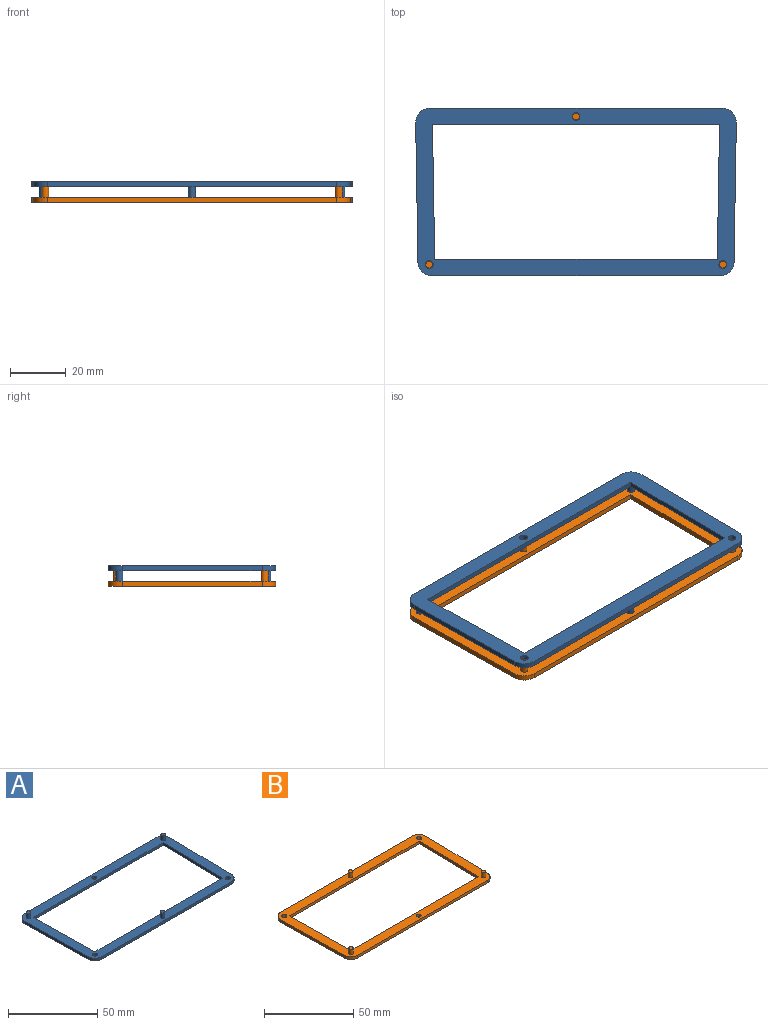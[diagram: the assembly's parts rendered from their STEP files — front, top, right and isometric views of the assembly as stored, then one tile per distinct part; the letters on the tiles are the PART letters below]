
ASSEMBLY  parts=2 mates=1
PART A: 23 faces, bbox 114.8x60x5.4 mm
  f0: plane 104.83x1.8mm, normal (0,1,0), area 188.7mm2, adj f8,f9,f21,f22
  f1: plane 50x1.8mm, normal (-1,-0.02,0), area 90mm2, adj f8,f9,f19,f22
  f2: plane 103.17x1.8mm, normal (0,-1,0), area 185.7mm2, adj f8,f9,f19,f20
  f3: plane 48x1.8mm, normal (1,0.02,0), area 86.4mm2, adj f4,f6,f8,f9
  f4: plane 102.8x1.8mm, normal (0,-1,0), area 185mm2, adj f3,f5,f8,f9
  f5: plane 48x1.8mm, normal (-1,0.02,0), area 86.4mm2, adj f4,f6,f8,f9
  f6: plane 101.2x1.8mm, normal (0,1,0), area 182.2mm2, adj f3,f5,f8,f9
  f7: plane 50x1.8mm, normal (1,-0.02,0), area 90mm2, adj f8,f9,f20,f21
  f8: plane 114.83x60mm, normal (0,0,1), area 1889.4mm2, adj f0,f1,f2,f3,f4,f5,f6,f7
  f9: plane 114.83x60mm, normal (0,0,-1), area 1904.1mm2, adj f0,f1,f2,f3,f4,f5,f6,f7
  f10: cylinder r=1.25mm len=3.6mm, axis (0,0,-1), area 28.3mm2, adj f8,f11
  f11: plane 2.5x2.5mm, normal (0,0,1), area 4.9mm2, adj f10
  f12: cylinder r=1.25mm len=3.6mm, axis (0,0,-1), area 28.3mm2, adj f8,f13
  f13: plane 2.5x2.5mm, normal (0,0,1), area 4.9mm2, adj f12
  f14: cylinder r=1.25mm len=3.6mm, axis (0,0,-1), area 28.3mm2, adj f8,f15
  f15: plane 2.5x2.5mm, normal (0,0,1), area 4.9mm2, adj f14
  f16: cylinder r=1.4mm len=2.8mm, axis (0,0,-1), area 15.8mm2, adj f8,f9
  f17: cylinder r=1.4mm len=2.8mm, axis (0,0,-1), area 15.8mm2, adj f8,f9
  f18: cylinder r=1.4mm len=2.8mm, axis (0,0,-1), area 15.8mm2, adj f8,f9
  f19: cylinder r=5mm len=5mm, axis (0,0,1), area 14mm2, adj f1,f2,f8,f9
  f20: cylinder r=5mm len=5mm, axis (0,0,1), area 14mm2, adj f2,f7,f8,f9
  f21: cylinder r=5mm len=5.08mm, axis (0,0,-1), area 14.3mm2, adj f0,f7,f8,f9
  f22: cylinder r=5mm len=5.08mm, axis (0,0,-1), area 14.3mm2, adj f0,f1,f8,f9
PART B: 23 faces, bbox 114.8x60x5.4 mm
  f0: plane 104.83x1.8mm, normal (0,1,0), area 188.7mm2, adj f8,f9,f21,f22
  f1: plane 50x1.8mm, normal (-1,-0.02,0), area 90mm2, adj f8,f9,f19,f22
  f2: plane 103.17x1.8mm, normal (0,-1,0), area 185.7mm2, adj f8,f9,f19,f20
  f3: plane 48x1.8mm, normal (1,0.02,0), area 86.4mm2, adj f4,f6,f8,f9
  f4: plane 102.8x1.8mm, normal (0,-1,0), area 185mm2, adj f3,f5,f8,f9
  f5: plane 48x1.8mm, normal (-1,0.02,0), area 86.4mm2, adj f4,f6,f8,f9
  f6: plane 101.2x1.8mm, normal (0,1,0), area 182.2mm2, adj f3,f5,f8,f9
  f7: plane 50x1.8mm, normal (1,-0.02,0), area 90mm2, adj f8,f9,f20,f21
  f8: plane 114.83x60mm, normal (0,0,1), area 1889.4mm2, adj f0,f1,f2,f3,f4,f5,f6,f7
  f9: plane 114.83x60mm, normal (0,0,-1), area 1904.1mm2, adj f0,f1,f2,f3,f4,f5,f6,f7
  f10: cylinder r=1.4mm len=2.8mm, axis (0,0,-1), area 15.8mm2, adj f8,f9
  f11: cylinder r=1.4mm len=2.8mm, axis (0,0,-1), area 15.8mm2, adj f8,f9
  f12: cylinder r=1.4mm len=2.8mm, axis (0,0,-1), area 15.8mm2, adj f8,f9
  f13: cylinder r=1.25mm len=3.6mm, axis (0,0,-1), area 28.3mm2, adj f8,f14
  f14: plane 2.5x2.5mm, normal (0,0,1), area 4.9mm2, adj f13
  f15: cylinder r=1.25mm len=3.6mm, axis (0,0,-1), area 28.3mm2, adj f8,f16
  f16: plane 2.5x2.5mm, normal (0,0,1), area 4.9mm2, adj f15
  f17: cylinder r=1.25mm len=3.6mm, axis (0,0,-1), area 28.3mm2, adj f8,f18
  f18: plane 2.5x2.5mm, normal (0,0,1), area 4.9mm2, adj f17
  f19: cylinder r=5mm len=5mm, axis (0,0,1), area 14mm2, adj f1,f2,f8,f9
  f20: cylinder r=5mm len=5mm, axis (0,0,1), area 14mm2, adj f2,f7,f8,f9
  f21: cylinder r=5mm len=5.08mm, axis (0,0,-1), area 14.3mm2, adj f0,f7,f8,f9
  f22: cylinder r=5mm len=5.08mm, axis (0,0,-1), area 14.3mm2, adj f0,f1,f8,f9
PLACE A rot(axis=(0,1,0),180deg) t=(-0.07,0,93.63)mm
PLACE B rot(axis=(0.95,0.22,-0.22),0deg) t=(-0.07,0,86.43)mm
MATE pin_slot B.f11 <-> A.f10  axis (0,0,-1) through (53.36,26,88.23)mm
